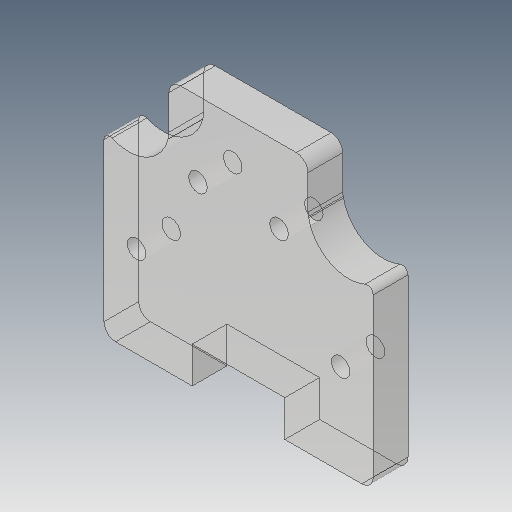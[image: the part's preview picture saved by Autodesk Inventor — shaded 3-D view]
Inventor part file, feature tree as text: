
AUTODESK INVENTOR PART (.ipt)
format: ipt  version: 2017 (Build 210142000, 142)  size: 194,560 bytes
history: native  units: in
note: dims shown in document units (in); Inventor stores cm internally (conversion verified against a paired STEP export)
features: extrude x4, sketch x4, reference x3, other x3, fillet x2, plane x1
ambient origin geometry x8: Origin, YZ Plane, XZ Plane, XY Plane, X Axis, Y Axis, Z Axis, Center Point
bodies: Solid1 (feature_tree)
feature tree (17):
  extrude  "Extrusion1"  Depth=0.2362in TaperAngle=0.0deg
  extrude  "Extrusion2"  Depth=0.0787in
  fillet  "Fillet1"  Radius=0.315in
  fillet  "Fillet2"  [1 undecoded]
  extrude  "Extrusion3"  TaperAngle=0.0deg  [1 undecoded]
  sketch  "Sketch4"  dims[d10=0.3937in d11=0.0in d12=0.3937in d13=0.0in]
  plane  "Work Plane1"
  extrude  "Extrusion4"  Depth=0.3937in TaperAngle=0.0deg
  sketch  "Sketch1"  dims[d0=0.2362in d1=0.0in d2=0.2362in d3=0.0in]
  sketch  "Sketch2"  dims[d4=0.0394in d5=0.0787in d6=0.315in d7=180.0deg]
  reference  "Reference1"
  reference  "Reference2"
  sketch  "Sketch3"  dims[d8=0.6299in d9=0.0in]
  reference  "Reference3"
  other  "<userpath>\OneDrive\Inventor\Beast 3D Printer\Hotend Mount Assembly.iam"
  other  "Hotend Mount Assembly.iam"
  other  "Hotend Slide Part 2:1"
note: 2 required parameter values undecoded (feature->parameter linkage not recoverable at this tier; creation-order binding heuristic only, values carry confidence <= 0.55)
